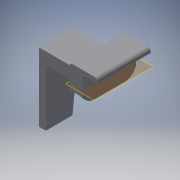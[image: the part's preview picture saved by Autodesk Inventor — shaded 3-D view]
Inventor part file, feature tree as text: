
AUTODESK INVENTOR PART (.ipt)
format: ipt  version: 2018 (Build 220112000, 112)  size: 219,648 bytes
history: native  units: in
note: dims shown in document units (in); Inventor stores cm internally (conversion verified against a paired STEP export)
features: extrude x7, sketch x7, fillet x6, other x2, plane x1, reference x1
ambient origin geometry x8: Origin, YZ Plane, XZ Plane, XY Plane, X Axis, Y Axis, Z Axis, Center Point
bodies: Solid1 (feature_tree)
feature tree (24):
  extrude  "Extrusion1"  Depth=0.6in
  plane  "Work Plane1"
  extrude  "Extrusion2"  Depth=0.05in TaperAngle=0.0deg
  extrude  "Extrusion3"  Depth=0.05in TaperAngle=0.0deg
  extrude  "Extrusion4"  Depth=0.05in TaperAngle=0.0deg
  extrude  "Extrusion5"  Depth=0.0394in
  fillet  "Fillet1"  Radius=0.0394in
  fillet  "Fillet2"  Radius=0.125in
  fillet  "Fillet3"  Radius=0.25in
  fillet  "Fillet4"  Radius=1.0in
  extrude  "Extrusion7"  Depth=0.0394in
  extrude  "Extrusion8"  [1 undecoded]
  fillet  "Fillet5"  [1 undecoded]
  fillet  "Fillet6"  [1 undecoded]
  sketch  "Sketch1"  dims[d0=0.3in d1=0.6in]
  sketch  "Sketch3"  dims[d2=0.3in d3=0.0in d4=0.05in d5=0.0in]
  sketch  "Sketch4"  dims[d6=2.0in d7=0.05in d8=0.0in]
  sketch  "Sketch5"  dims[d9=0.15in d10=0.0in d11=0.05in d12=0.0in]
  sketch  "Sketch6"  dims[d17=0.125in d18=0.0394in d19=0.0394in d20=0.125in d21=0.25in d22=1.0in d23=0.0in]
  sketch  "Sketch8"  dims[d24=0.0787in d25=0.0in d26=0.0394in]
  sketch  "Sketch9"  dims[d27=0.0394in]
  reference  "Reference1"
  other  "ArmTruss.iam"
  other  "bottomARM:1"
note: 3 required parameter values undecoded (feature->parameter linkage not recoverable at this tier; creation-order binding heuristic only, values carry confidence <= 0.55)
